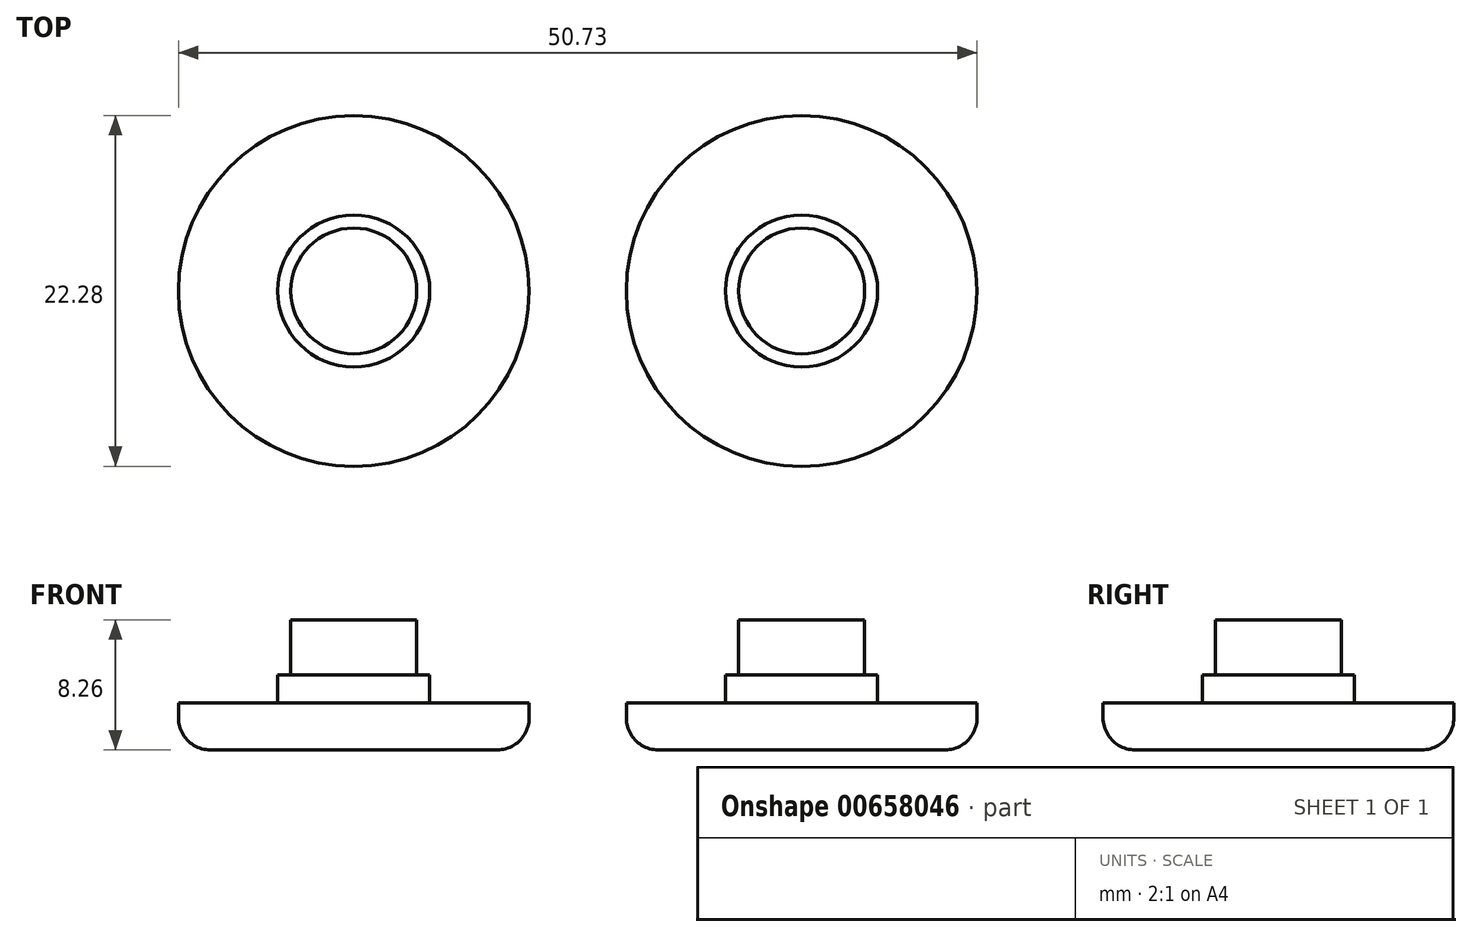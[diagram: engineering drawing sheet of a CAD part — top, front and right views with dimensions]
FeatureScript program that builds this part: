
annotation { "Feature Type Name" : "Feature", "Feature Type Description" : "" }
export const myFeature = defineFeature(function(context is Context, id is Id, definition is map)
    precondition{}
    {
        {
            var Q0;
            Q0=qCreatedBy(makeId("Top.planeOp"),FACE);
            var sketch = newSketch(context, id + "F0", { "sketchPlane" : qUnion([Q0])});
            skCircle(sketch, "E0", {"center": v(0, 0) * mm, "radius": 11.14 * mm});
            skSolve(sketch);
        }
        {
            var Q0;
            Q0=makeQuery(id+"F0.imprint","IMPRINT",FACE,{"disambiguationData":[TD([[makeQuery(id+"F0.imprint","IMPRINT",EDGE,{"derivedFrom":sQuery(id+"F0.wireOp",EDGE,"E0")}),1.0]])]});
            extrude(context, id + "F1", {"entities" : qUnion([Q0]), "oppositeDirection" : true, "depth" : 3 * mm, "offsetDistance" : 25.4 * mm});
        }
        {
            var Q0;
            Q0=makeQuery(id+"F1.opExtrude","CAP_FACE",FACE,{"disambiguationData":[OSD([sQuery(id+"F0.wireOp",EDGE,"E0")])],"isStart":true});
            var sketch = newSketch(context, id + "F2", { "sketchPlane" : qUnion([Q0])});
            skCircle(sketch, "E1", {"center": v(0, 0) * mm, "radius": 4.83 * mm});
            skSolve(sketch);
        }
        {
            var Q0;
            Q0=makeQuery(id+"F2.imprint","IMPRINT",FACE,{"disambiguationData":[TD([[makeQuery(id+"F2.imprint","IMPRINT",EDGE,{"derivedFrom":sQuery(id+"F2.wireOp",EDGE,"E1")}),1.0]])]});
            extrude(context, id + "F3", {"entities" : qUnion([Q0]), "operationType" : NewBodyOperationType.ADD, "depth" : 1.78 * mm, "offsetDistance" : 25.4 * mm});
        }
        {
            var Q0;
            Q0=makeQuery(id+"F3.opExtrude","CAP_FACE",FACE,{"disambiguationData":[OSD([sQuery(id+"F2.wireOp",EDGE,"E1")])],"isStart":false});
            var sketch = newSketch(context, id + "F4", { "sketchPlane" : qUnion([Q0])});
            skCircle(sketch, "E2", {"center": v(0, 0) * mm, "radius": 4 * mm});
            skSolve(sketch);
        }
        {
            var Q0;
            Q0=makeQuery(id+"F4.imprint","IMPRINT",FACE,{"disambiguationData":[TD([[makeQuery(id+"F4.imprint","IMPRINT",EDGE,{"derivedFrom":sQuery(id+"F4.wireOp",EDGE,"E2")}),1.0]])]});
            extrude(context, id + "F5", {"entities" : qUnion([Q0]), "operationType" : NewBodyOperationType.ADD, "depth" : 3.48 * mm, "offsetDistance" : 25.4 * mm});
        }
        {
            var Q0;
            Q0=makeQuery(id+"F1.opExtrude","SWEPT_BODY",BODY,{"disambiguationData":[OSD([sQuery(id+"F0.wireOp",EDGE,"E0")])]});
            transform(context, id + "F6", {"entities" : qUnion([Q0]), "transformType" : TransformType.TRANSLATION_3D, "dx" : 28.45 * mm, "dy" : 0 * mm, "dz" : 0 * mm, "makeCopy" : true});
        }
        {
            var Q0;
            Q0=makeQuery(id+"F1.opExtrude","CAP_EDGE",EDGE,{"disambiguationData":[OSD([sQuery(id+"F0.wireOp",EDGE,"E0")])],"isStart":false});
            var Q1;
            Q1=makeQuery(id+"F6.opPattern","COPY",EDGE,{"derivedFrom":makeQuery(id+"F1.opExtrude","CAP_EDGE",EDGE,{"disambiguationData":[OSD([sQuery(id+"F0.wireOp",EDGE,"E0")])],"isStart":false}),"instanceName":"1"});
            fillet(context, id + "F7", {"entities" : qUnion([Q0, Q1]), "radius" : 2.03 * mm, "tangentPropagation" : true, "allowEdgeOverflow" : false});
        }
    });
